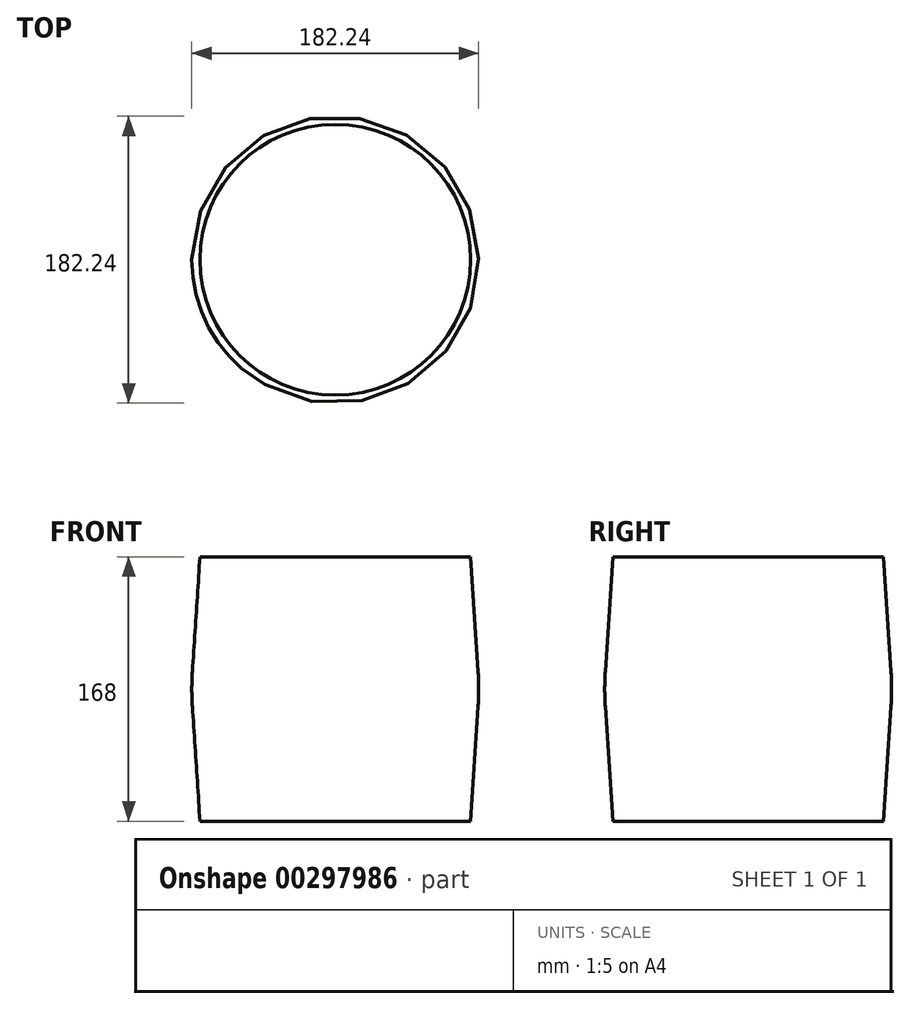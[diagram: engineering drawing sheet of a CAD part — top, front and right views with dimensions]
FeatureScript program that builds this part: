
annotation { "Feature Type Name" : "Feature", "Feature Type Description" : "" }
export const myFeature = defineFeature(function(context is Context, id is Id, definition is map)
    precondition{}
    {
        {
            var Q0;
            Q0=qCreatedBy(makeId("Front.planeOp"),FACE);
            var sketch = newSketch(context, id + "F0", { "sketchPlane" : qUnion([Q0])});
            skLineSegment(sketch, "E0", {"start": v(0, -65.3) * mm, "end": v(0, 102.7) * mm});
            skLineSegment(sketch, "E1", {"start": v(0, 102.7) * mm, "end": v(85.95, 102.7) * mm});
            skLineSegment(sketch, "E2", {"start": v(85.95, 102.7) * mm, "end": v(91.48, 18.7) * mm});
            skLineSegment(sketch, "E3", {"start": v(91.48, 18.7) * mm, "end": v(85.95, -65.3) * mm});
            skLineSegment(sketch, "E4", {"start": v(85.95, -65.3) * mm, "end": v(0, -65.3) * mm});
            skLineSegment(sketch, "E5", {"start": v(85.95, 102.7) * mm, "end": v(85.95, -65.3) * mm});
            skPoint(sketch, "E6", {"position": v(85.95, 18.7) * mm});
            skLineSegment(sketch, "E7", {"start": v(91.48, 18.7) * mm, "end": v(85.95, 18.7) * mm, "construction": true});
            skSolve(sketch);
        }
        {
            var Q0;
            Q0=makeQuery(id+"F0.imprint","IMPRINT",FACE,{"disambiguationData":[TD([[makeQuery(id+"F0.imprint","IMPRINT",EDGE,{"derivedFrom":sQuery(id+"F0.wireOp",EDGE,"E2")}),-1.0]])]});
            var Q1;
            Q1=makeQuery(id+"F0.imprint","IMPRINT",FACE,{"disambiguationData":[TD([[makeQuery(id+"F0.imprint","IMPRINT",EDGE,{"derivedFrom":sQuery(id+"F0.wireOp",EDGE,"E0")}),-1.0]])]});
            var Q2;
            Q2=sQuery(id+"F0.wireOp",EDGE,"E0");
            revolve(context, id + "F1", {"entities" : qUnion([Q0, Q1]), "axis" : qUnion([Q2]), "revolveType" : RevolveType.FULL});
        }
        {
            var Q0;
            Q0=makeQuery(id+"F1.opRevolve","SWEPT_EDGE",EDGE,{"disambiguationData":[OSD([sQuery(id+"F0.wireOp",EDGE,"E2"),sQuery(id+"F0.wireOp",EDGE,"E3")])]});
            fillet(context, id + "F2", {"entities" : qUnion([Q0]), "radius" : 168 * mm, "tangentPropagation" : true, "allowEdgeOverflow" : false});
        }
    });
